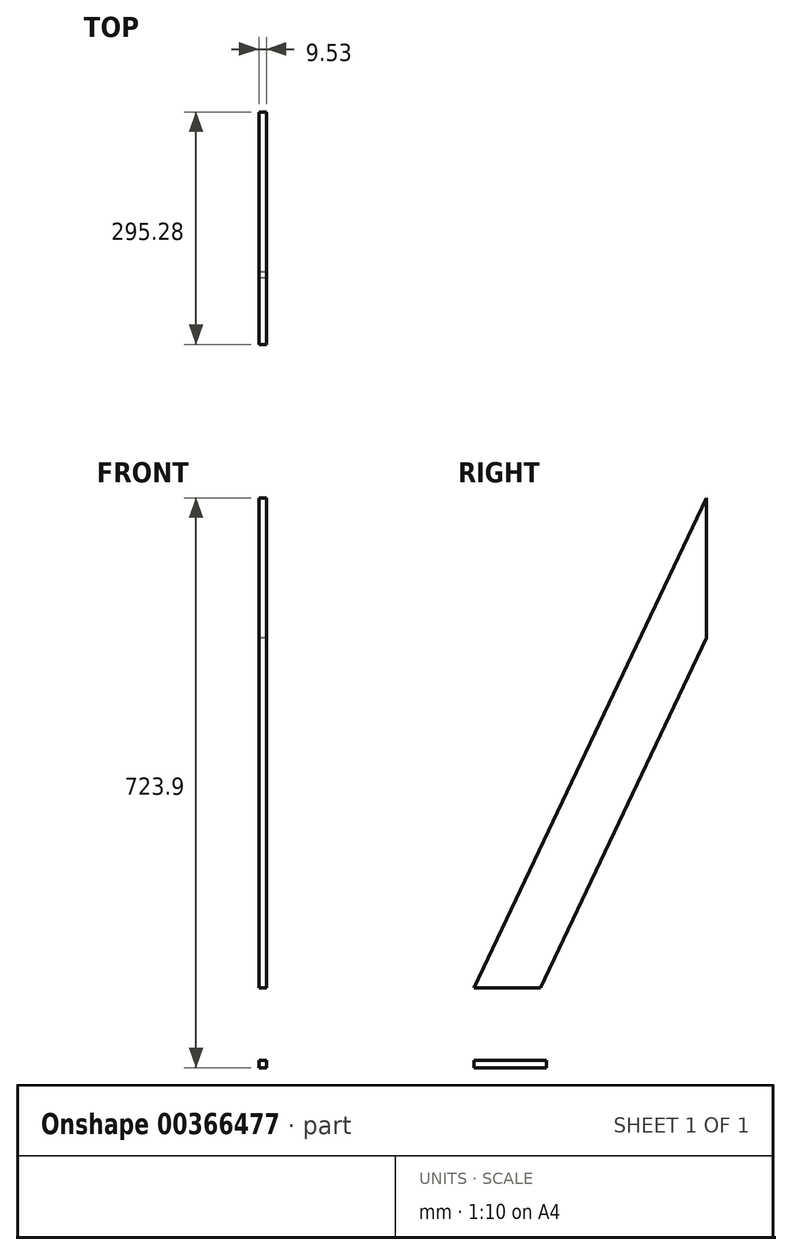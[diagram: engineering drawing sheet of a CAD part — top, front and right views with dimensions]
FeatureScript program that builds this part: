
annotation { "Feature Type Name" : "Feature", "Feature Type Description" : "" }
export const myFeature = defineFeature(function(context is Context, id is Id, definition is map)
    precondition{}
    {
        {
            var Q0;
            Q0=qCreatedBy(makeId("Right.planeOp"),FACE);
            var sketch = newSketch(context, id + "F0", { "sketchPlane" : qUnion([Q0])});
            skLineSegment(sketch, "E0.bottom", {"start": v(0, 0) * mm, "end": v(-381, 0) * mm});
            skLineSegment(sketch, "E0.top", {"start": v(0, 723.9) * mm, "end": v(-381, 723.9) * mm});
            skLineSegment(sketch, "E0.left", {"start": v(0, 0) * mm, "end": v(0, 723.9) * mm});
            skLineSegment(sketch, "E0.right", {"start": v(-381, 0) * mm, "end": v(-381, 723.9) * mm});
            skLineSegment(sketch, "E1.bottom", {"start": v(-381, 0) * mm, "end": v(-371.48, 0) * mm});
            skLineSegment(sketch, "E1.top", {"start": v(-381, 101.6) * mm, "end": v(-371.48, 101.6) * mm});
            skLineSegment(sketch, "E1.left", {"start": v(-381, 0) * mm, "end": v(-381, 101.6) * mm});
            skLineSegment(sketch, "E1.right", {"start": v(-371.48, 0) * mm, "end": v(-371.48, 101.6) * mm});
            skLineSegment(sketch, "E2.bottom", {"start": v(-371.48, 9.52) * mm, "end": v(-279.4, 9.52) * mm});
            skLineSegment(sketch, "E2.top", {"start": v(-371.48, 0) * mm, "end": v(-279.4, 0) * mm});
            skLineSegment(sketch, "E2.left", {"start": v(-371.48, 9.52) * mm, "end": v(-371.48, 0) * mm});
            skLineSegment(sketch, "E2.right", {"start": v(-279.4, 9.52) * mm, "end": v(-279.4, 0) * mm});
            skLineSegment(sketch, "E3.bottom", {"start": v(0, 723.9) * mm, "end": v(-76.2, 723.9) * mm});
            skLineSegment(sketch, "E3.top", {"start": v(0, 0) * mm, "end": v(-76.2, 0) * mm});
            skLineSegment(sketch, "E3.left", {"start": v(0, 723.9) * mm, "end": v(0, 0) * mm});
            skLineSegment(sketch, "E3.right", {"start": v(-76.2, 723.9) * mm, "end": v(-76.2, 0) * mm});
            skLineSegment(sketch, "E4.bottom", {"start": v(-76.2, 101.6) * mm, "end": v(-85.73, 101.6) * mm});
            skLineSegment(sketch, "E4.top", {"start": v(-76.2, 0) * mm, "end": v(-85.73, 0) * mm});
            skLineSegment(sketch, "E4.left", {"start": v(-76.2, 101.6) * mm, "end": v(-76.2, 0) * mm});
            skLineSegment(sketch, "E4.right", {"start": v(-85.73, 101.6) * mm, "end": v(-85.73, 0) * mm});
            skLineSegment(sketch, "E5.bottom", {"start": v(-85.73, 9.53) * mm, "end": v(-177.8, 9.53) * mm});
            skLineSegment(sketch, "E5.top", {"start": v(-85.73, 0) * mm, "end": v(-177.8, 0) * mm});
            skLineSegment(sketch, "E5.left", {"start": v(-85.73, 9.53) * mm, "end": v(-85.73, 0) * mm});
            skLineSegment(sketch, "E5.right", {"start": v(-177.8, 9.53) * mm, "end": v(-177.8, 0) * mm});
            skLineSegment(sketch, "E6", {"start": v(-371.48, 101.6) * mm, "end": v(-76.2, 723.9) * mm});
            skLineSegment(sketch, "E7", {"start": v(-279.4, 9.52) * mm, "end": v(-177.8, 9.53) * mm});
            skLineSegment(sketch, "E8", {"start": v(-371.48, 101.6) * mm, "end": v(-85.73, 101.6) * mm});
            skLineSegment(sketch, "E9.0", {"start": v(-287.13, 101.6) * mm, "end": v(-76.2, 546.15) * mm});
            skSolve(sketch);
        }
        {
            var Q0;
            {var subQ0=sQuery(id+"F0.wireOp",EDGE,"E6");Q0=makeQuery(id+"F0.imprint","IMPRINT",FACE,{"disambiguationData":[TD([[makeQuery(id+"F0.imprint","IMPRINT",EDGE,{"derivedFrom":subQ0}),-1.0]])]});}
            var Q1;
            {var subQ1=sQuery(id+"F0.wireOp",EDGE,"E1.right");Q1=makeQuery(id+"F0.imprint","IMPRINT",FACE,{"disambiguationData":[TD([[makeQuery(id+"F0.imprint","IMPRINT",EDGE,{"derivedFrom":subQ1}),-1.0]])]});}
            extrude(context, id + "F1", {"entities" : qUnion([Q0, Q1]), "depth" : 9.52 * mm});
        }
    });
